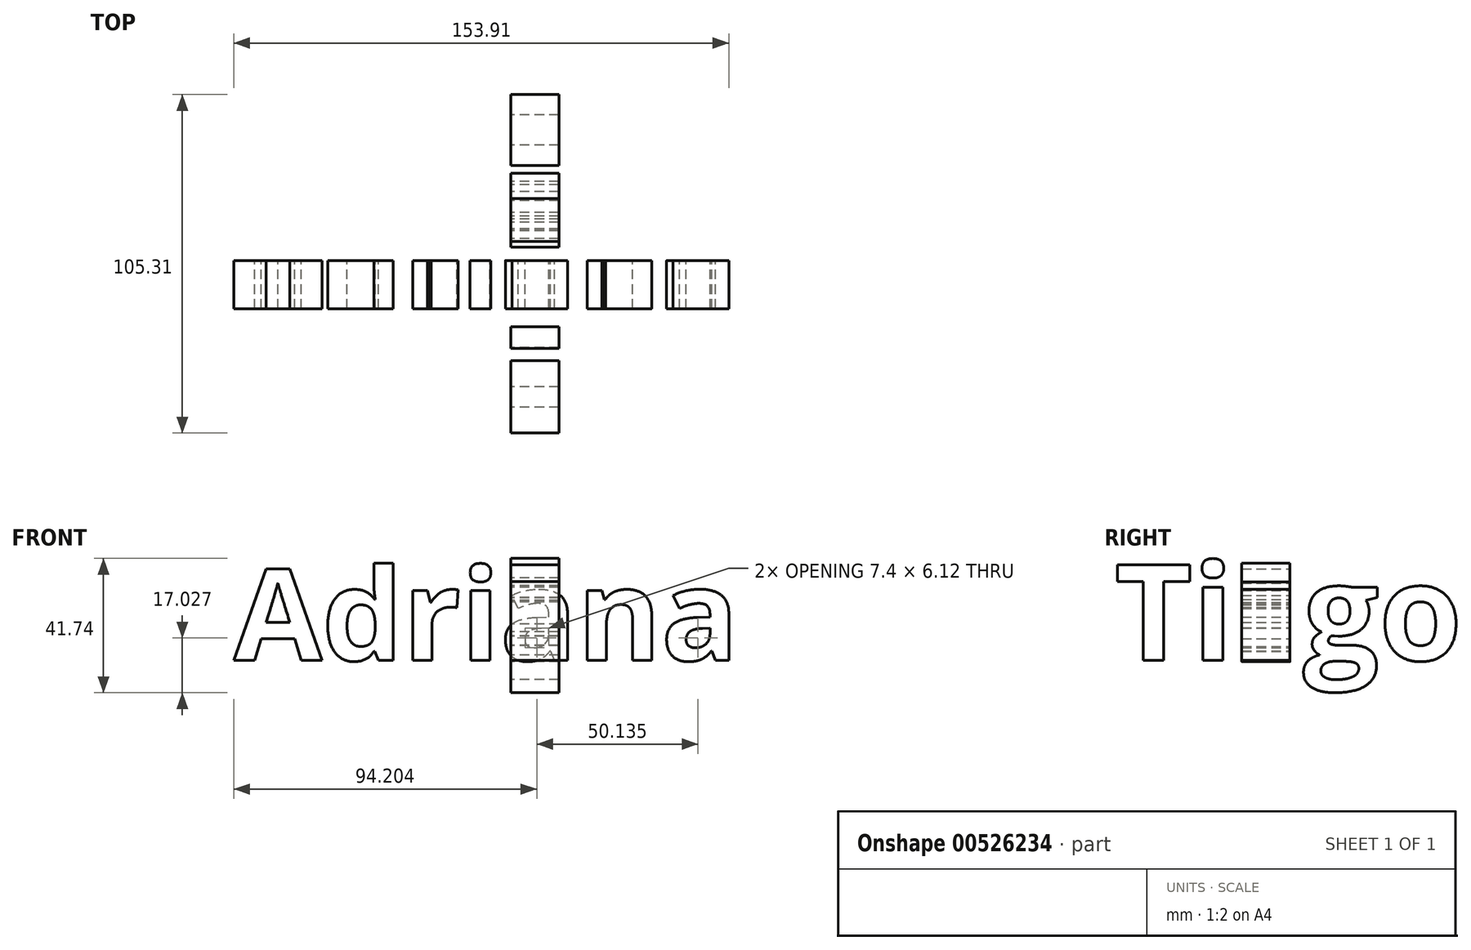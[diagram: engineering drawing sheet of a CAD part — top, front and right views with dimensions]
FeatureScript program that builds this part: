
annotation { "Feature Type Name" : "Feature", "Feature Type Description" : "" }
export const myFeature = defineFeature(function(context is Context, id is Id, definition is map)
    precondition{}
    {
        {
            var Q0;
            Q0=qCreatedBy(makeId("Front.planeOp"),FACE);
            var sketch = newSketch(context, id + "F0", { "sketchPlane" : qUnion([Q0])});
            skText(sketch, "E0", { "text": "Adriana", "fontName": "OpenSans-Bold.ttf"});
            const initialGuessF0  = {"E0": [-0.08609, 0, 1, 0, 0.02862]};
            skSetInitialGuess(sketch, initialGuessF0);
            skSolve(sketch);
        }
        {
            var Q0;
            Q0 = qSketchRegion(id + "F0", true);
            extrude(context, id + "F1", {"entities" : qUnion([Q0]), "depth" : 15 * mm, "offsetDistance" : 25 * mm});
        }
        {
            var Q0;
            Q0=qCreatedBy(makeId("Right.planeOp"),FACE);
            var sketch = newSketch(context, id + "F2", { "sketchPlane" : qUnion([Q0])});
            skText(sketch, "E1", { "text": "Ti  go", "fontName": "OpenSans-Bold.ttf"});
            const initialGuessF2  = {"E1": [-0.0545, 0, 1, 0, 0.03005]};
            skSetInitialGuess(sketch, initialGuessF2);
            skSolve(sketch);
        }
        {
            var Q0;
            Q0 = qSketchRegion(id + "F2", true);
            extrude(context, id + "F3", {"entities" : qUnion([Q0]), "depth" : 15 * mm, "offsetDistance" : 25 * mm});
        }
    });
